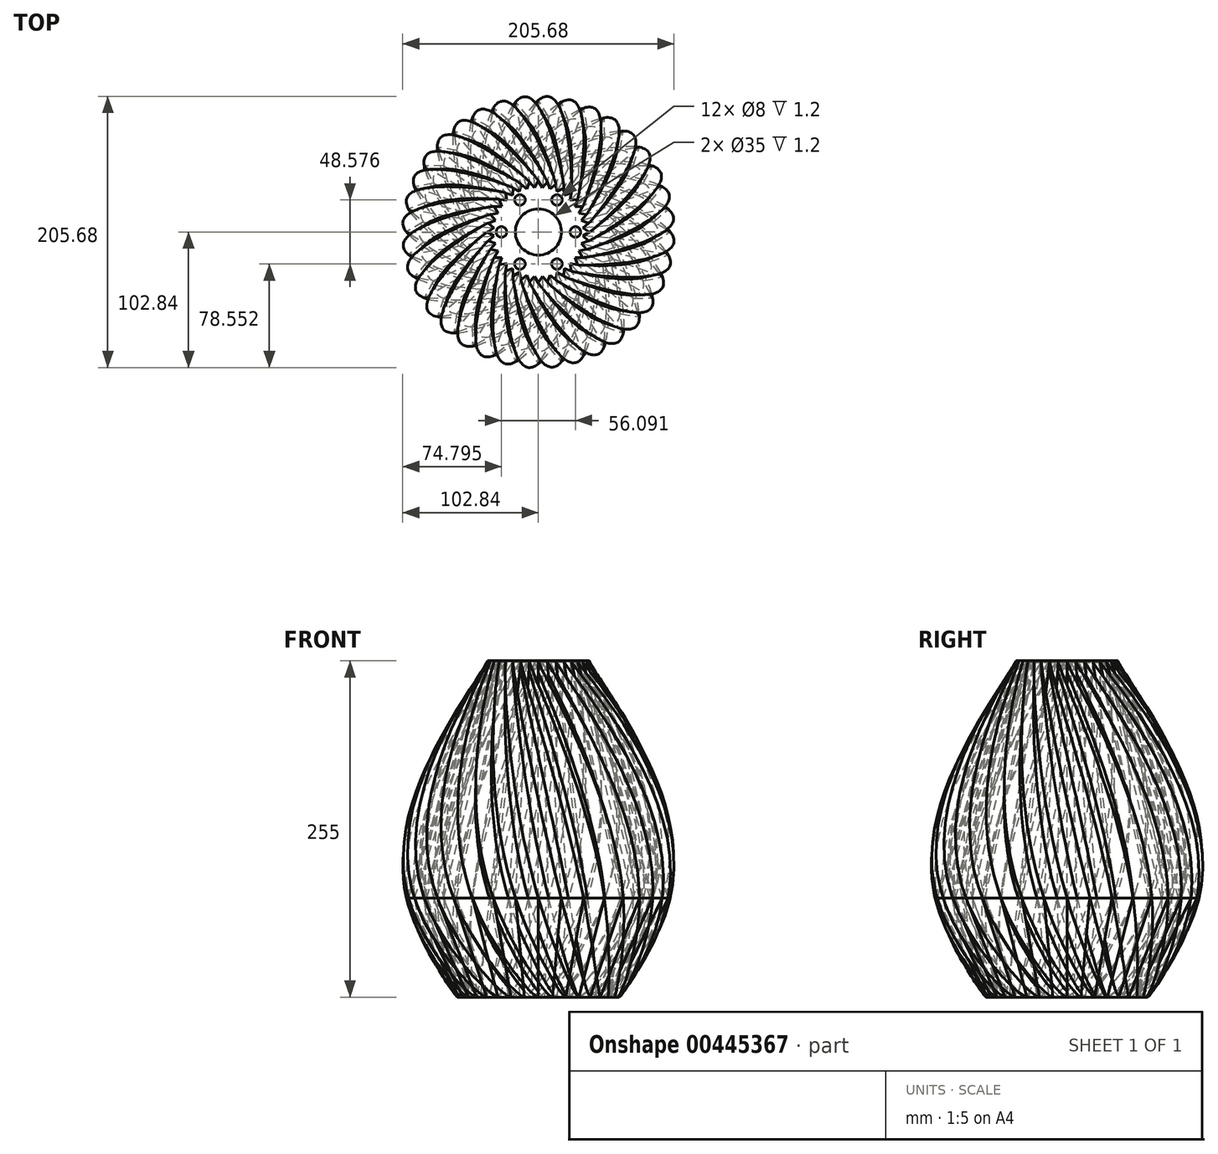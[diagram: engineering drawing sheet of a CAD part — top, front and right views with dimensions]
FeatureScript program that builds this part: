
annotation { "Feature Type Name" : "Feature", "Feature Type Description" : "" }
export const myFeature = defineFeature(function(context is Context, id is Id, definition is map)
    precondition{}
    {
        {
            var Q0;
            Q0=qCreatedBy(makeId("Top.planeOp"),FACE);
            var sketch = newSketch(context, id + "F0", { "sketchPlane" : qUnion([Q0])});
            skCircle(sketch, "E0", {"center": v(0, 0) * mm, "radius": 100 * mm, "construction": true});
            skLineSegment(sketch, "E1", {"start": v(-7.64, 87.34) * mm, "end": v(0, 100) * mm});
            skLineSegment(sketch, "E2.MirrorCS", {"start": v(7.64, 87.34) * mm, "end": v(0, 100) * mm});
            skLineSegment(sketch, "E3.1.0", {"start": v(-22.7, 84.69) * mm, "end": v(-17.36, 98.48) * mm});
            skLineSegment(sketch, "E3.1.1", {"start": v(-7.64, 87.34) * mm, "end": v(-17.36, 98.48) * mm});
            skLineSegment(sketch, "E3.2.0", {"start": v(-37.05, 79.46) * mm, "end": v(-34.2, 93.97) * mm});
            skLineSegment(sketch, "E3.2.1", {"start": v(-22.7, 84.69) * mm, "end": v(-34.2, 93.97) * mm});
            skLineSegment(sketch, "E3.3.0", {"start": v(-50.29, 71.82) * mm, "end": v(-50, 86.6) * mm});
            skLineSegment(sketch, "E3.3.1", {"start": v(-37.05, 79.46) * mm, "end": v(-50, 86.6) * mm});
            skLineSegment(sketch, "E3.4.0", {"start": v(-62, 62) * mm, "end": v(-64.28, 76.6) * mm});
            skLineSegment(sketch, "E3.4.1", {"start": v(-50.29, 71.82) * mm, "end": v(-64.28, 76.6) * mm});
            skLineSegment(sketch, "E3.5.0", {"start": v(-71.82, 50.29) * mm, "end": v(-76.6, 64.28) * mm});
            skLineSegment(sketch, "E3.5.1", {"start": v(-62, 62) * mm, "end": v(-76.6, 64.28) * mm});
            skLineSegment(sketch, "E3.6.0", {"start": v(-79.46, 37.05) * mm, "end": v(-86.6, 50) * mm});
            skLineSegment(sketch, "E3.6.1", {"start": v(-71.82, 50.29) * mm, "end": v(-86.6, 50) * mm});
            skLineSegment(sketch, "E3.7.0", {"start": v(-84.69, 22.7) * mm, "end": v(-93.97, 34.2) * mm});
            skLineSegment(sketch, "E3.7.1", {"start": v(-79.46, 37.05) * mm, "end": v(-93.97, 34.2) * mm});
            skLineSegment(sketch, "E3.8.0", {"start": v(-87.34, 7.64) * mm, "end": v(-98.48, 17.36) * mm});
            skLineSegment(sketch, "E3.8.1", {"start": v(-84.69, 22.7) * mm, "end": v(-98.48, 17.36) * mm});
            skLineSegment(sketch, "E3.9.0", {"start": v(-87.34, -7.64) * mm, "end": v(-100, 0) * mm});
            skLineSegment(sketch, "E3.9.1", {"start": v(-87.34, 7.64) * mm, "end": v(-100, 0) * mm});
            skLineSegment(sketch, "E3.10.0", {"start": v(-84.69, -22.7) * mm, "end": v(-98.48, -17.36) * mm});
            skLineSegment(sketch, "E3.10.1", {"start": v(-87.34, -7.64) * mm, "end": v(-98.48, -17.36) * mm});
            skLineSegment(sketch, "E3.11.0", {"start": v(-79.46, -37.05) * mm, "end": v(-93.97, -34.2) * mm});
            skLineSegment(sketch, "E3.11.1", {"start": v(-84.69, -22.7) * mm, "end": v(-93.97, -34.2) * mm});
            skLineSegment(sketch, "E3.12.0", {"start": v(-71.82, -50.29) * mm, "end": v(-86.6, -50) * mm});
            skLineSegment(sketch, "E3.12.1", {"start": v(-79.46, -37.05) * mm, "end": v(-86.6, -50) * mm});
            skLineSegment(sketch, "E3.13.0", {"start": v(-62, -62) * mm, "end": v(-76.6, -64.28) * mm});
            skLineSegment(sketch, "E3.13.1", {"start": v(-71.82, -50.29) * mm, "end": v(-76.6, -64.28) * mm});
            skLineSegment(sketch, "E3.14.0", {"start": v(-50.29, -71.82) * mm, "end": v(-64.28, -76.6) * mm});
            skLineSegment(sketch, "E3.14.1", {"start": v(-62, -62) * mm, "end": v(-64.28, -76.6) * mm});
            skLineSegment(sketch, "E3.15.0", {"start": v(-37.05, -79.46) * mm, "end": v(-50, -86.6) * mm});
            skLineSegment(sketch, "E3.15.1", {"start": v(-50.29, -71.82) * mm, "end": v(-50, -86.6) * mm});
            skLineSegment(sketch, "E3.16.0", {"start": v(-22.7, -84.69) * mm, "end": v(-34.2, -93.97) * mm});
            skLineSegment(sketch, "E3.16.1", {"start": v(-37.05, -79.46) * mm, "end": v(-34.2, -93.97) * mm});
            skLineSegment(sketch, "E3.17.0", {"start": v(-7.64, -87.34) * mm, "end": v(-17.36, -98.48) * mm});
            skLineSegment(sketch, "E3.17.1", {"start": v(-22.7, -84.69) * mm, "end": v(-17.36, -98.48) * mm});
            skLineSegment(sketch, "E3.18.0", {"start": v(7.64, -87.34) * mm, "end": v(0, -100) * mm});
            skLineSegment(sketch, "E3.18.1", {"start": v(-7.64, -87.34) * mm, "end": v(0, -100) * mm});
            skLineSegment(sketch, "E3.19.0", {"start": v(22.7, -84.69) * mm, "end": v(17.36, -98.48) * mm});
            skLineSegment(sketch, "E3.19.1", {"start": v(7.64, -87.34) * mm, "end": v(17.36, -98.48) * mm});
            skLineSegment(sketch, "E3.20.0", {"start": v(37.05, -79.46) * mm, "end": v(34.2, -93.97) * mm});
            skLineSegment(sketch, "E3.20.1", {"start": v(22.7, -84.69) * mm, "end": v(34.2, -93.97) * mm});
            skLineSegment(sketch, "E3.21.0", {"start": v(50.29, -71.82) * mm, "end": v(50, -86.6) * mm});
            skLineSegment(sketch, "E3.21.1", {"start": v(37.05, -79.46) * mm, "end": v(50, -86.6) * mm});
            skLineSegment(sketch, "E3.22.0", {"start": v(62, -62) * mm, "end": v(64.28, -76.6) * mm});
            skLineSegment(sketch, "E3.22.1", {"start": v(50.29, -71.82) * mm, "end": v(64.28, -76.6) * mm});
            skLineSegment(sketch, "E3.23.0", {"start": v(71.82, -50.29) * mm, "end": v(76.6, -64.28) * mm});
            skLineSegment(sketch, "E3.23.1", {"start": v(62, -62) * mm, "end": v(76.6, -64.28) * mm});
            skLineSegment(sketch, "E3.24.0", {"start": v(79.46, -37.05) * mm, "end": v(86.6, -50) * mm});
            skLineSegment(sketch, "E3.24.1", {"start": v(71.82, -50.29) * mm, "end": v(86.6, -50) * mm});
            skLineSegment(sketch, "E3.25.0", {"start": v(84.69, -22.7) * mm, "end": v(93.97, -34.2) * mm});
            skLineSegment(sketch, "E3.25.1", {"start": v(79.46, -37.05) * mm, "end": v(93.97, -34.2) * mm});
            skLineSegment(sketch, "E3.26.0", {"start": v(87.34, -7.64) * mm, "end": v(98.48, -17.36) * mm});
            skLineSegment(sketch, "E3.26.1", {"start": v(84.69, -22.7) * mm, "end": v(98.48, -17.36) * mm});
            skLineSegment(sketch, "E3.27.0", {"start": v(87.34, 7.64) * mm, "end": v(100, 0) * mm});
            skLineSegment(sketch, "E3.27.1", {"start": v(87.34, -7.64) * mm, "end": v(100, 0) * mm});
            skLineSegment(sketch, "E3.28.0", {"start": v(84.69, 22.7) * mm, "end": v(98.48, 17.36) * mm});
            skLineSegment(sketch, "E3.28.1", {"start": v(87.34, 7.64) * mm, "end": v(98.48, 17.36) * mm});
            skLineSegment(sketch, "E3.29.0", {"start": v(79.46, 37.05) * mm, "end": v(93.97, 34.2) * mm});
            skLineSegment(sketch, "E3.29.1", {"start": v(84.69, 22.7) * mm, "end": v(93.97, 34.2) * mm});
            skLineSegment(sketch, "E3.30.0", {"start": v(71.82, 50.29) * mm, "end": v(86.6, 50) * mm});
            skLineSegment(sketch, "E3.30.1", {"start": v(79.46, 37.05) * mm, "end": v(86.6, 50) * mm});
            skLineSegment(sketch, "E3.31.0", {"start": v(62, 62) * mm, "end": v(76.6, 64.28) * mm});
            skLineSegment(sketch, "E3.31.1", {"start": v(71.82, 50.29) * mm, "end": v(76.6, 64.28) * mm});
            skLineSegment(sketch, "E3.32.0", {"start": v(50.29, 71.82) * mm, "end": v(64.28, 76.6) * mm});
            skLineSegment(sketch, "E3.32.1", {"start": v(62, 62) * mm, "end": v(64.28, 76.6) * mm});
            skLineSegment(sketch, "E3.33.0", {"start": v(37.05, 79.46) * mm, "end": v(50, 86.6) * mm});
            skLineSegment(sketch, "E3.33.1", {"start": v(50.29, 71.82) * mm, "end": v(50, 86.6) * mm});
            skLineSegment(sketch, "E3.34.0", {"start": v(22.7, 84.69) * mm, "end": v(34.2, 93.97) * mm});
            skLineSegment(sketch, "E3.34.1", {"start": v(37.05, 79.46) * mm, "end": v(34.2, 93.97) * mm});
            skLineSegment(sketch, "E3.35.0", {"start": v(7.64, 87.34) * mm, "end": v(17.36, 98.48) * mm});
            skLineSegment(sketch, "E3.35.1", {"start": v(22.7, 84.69) * mm, "end": v(17.36, 98.48) * mm});
            skSolve(sketch);
        }
        {
            var Q0;
            Q0=makeQuery(id+"F0.imprint","IMPRINT",FACE,{"disambiguationData":[TD([[makeQuery(id+"F0.imprint","IMPRINT",EDGE,{"derivedFrom":sQuery(id+"F0.wireOp",EDGE,"E1")}),-1.0]])]});
            extrude(context, id + "F1", {"entities" : qUnion([Q0]), "depth" : 180 * mm, "hasDraft" : true, "draftAngle" : 10 * degree, "draftPullDirection" : true});
        }
        {
            var Q1;
            Q1=makeQuery(id+"F1.opExtrude","CAP_FACE",FACE,{"disambiguationData":[OSD([sQuery(id+"F0.wireOp",EDGE,"E1"),sQuery(id+"F0.wireOp",EDGE,"E2.MirrorCS"),sQuery(id+"F0.wireOp",EDGE,"E3.1.0"),sQuery(id+"F0.wireOp",EDGE,"E3.1.1"),sQuery(id+"F0.wireOp",EDGE,"E3.2.0"),sQuery(id+"F0.wireOp",EDGE,"E3.2.1"),sQuery(id+"F0.wireOp",EDGE,"E3.3.0"),sQuery(id+"F0.wireOp",EDGE,"E3.3.1"),sQuery(id+"F0.wireOp",EDGE,"E3.4.0"),sQuery(id+"F0.wireOp",EDGE,"E3.4.1"),sQuery(id+"F0.wireOp",EDGE,"E3.5.0"),sQuery(id+"F0.wireOp",EDGE,"E3.5.1"),sQuery(id+"F0.wireOp",EDGE,"E3.6.0"),sQuery(id+"F0.wireOp",EDGE,"E3.6.1"),sQuery(id+"F0.wireOp",EDGE,"E3.7.0"),sQuery(id+"F0.wireOp",EDGE,"E3.7.1"),sQuery(id+"F0.wireOp",EDGE,"E3.8.0"),sQuery(id+"F0.wireOp",EDGE,"E3.8.1"),sQuery(id+"F0.wireOp",EDGE,"E3.9.0"),sQuery(id+"F0.wireOp",EDGE,"E3.9.1"),sQuery(id+"F0.wireOp",EDGE,"E3.10.0"),sQuery(id+"F0.wireOp",EDGE,"E3.10.1"),sQuery(id+"F0.wireOp",EDGE,"E3.11.0"),sQuery(id+"F0.wireOp",EDGE,"E3.11.1"),sQuery(id+"F0.wireOp",EDGE,"E3.12.0"),sQuery(id+"F0.wireOp",EDGE,"E3.12.1"),sQuery(id+"F0.wireOp",EDGE,"E3.13.0"),sQuery(id+"F0.wireOp",EDGE,"E3.13.1"),sQuery(id+"F0.wireOp",EDGE,"E3.14.0"),sQuery(id+"F0.wireOp",EDGE,"E3.14.1"),sQuery(id+"F0.wireOp",EDGE,"E3.15.0"),sQuery(id+"F0.wireOp",EDGE,"E3.15.1"),sQuery(id+"F0.wireOp",EDGE,"E3.16.0"),sQuery(id+"F0.wireOp",EDGE,"E3.16.1"),sQuery(id+"F0.wireOp",EDGE,"E3.17.0"),sQuery(id+"F0.wireOp",EDGE,"E3.17.1"),sQuery(id+"F0.wireOp",EDGE,"E3.18.0"),sQuery(id+"F0.wireOp",EDGE,"E3.18.1"),sQuery(id+"F0.wireOp",EDGE,"E3.19.0"),sQuery(id+"F0.wireOp",EDGE,"E3.19.1"),sQuery(id+"F0.wireOp",EDGE,"E3.20.0"),sQuery(id+"F0.wireOp",EDGE,"E3.20.1"),sQuery(id+"F0.wireOp",EDGE,"E3.21.0"),sQuery(id+"F0.wireOp",EDGE,"E3.21.1"),sQuery(id+"F0.wireOp",EDGE,"E3.22.0"),sQuery(id+"F0.wireOp",EDGE,"E3.22.1"),sQuery(id+"F0.wireOp",EDGE,"E3.23.0"),sQuery(id+"F0.wireOp",EDGE,"E3.23.1"),sQuery(id+"F0.wireOp",EDGE,"E3.24.0"),sQuery(id+"F0.wireOp",EDGE,"E3.24.1"),sQuery(id+"F0.wireOp",EDGE,"E3.25.0"),sQuery(id+"F0.wireOp",EDGE,"E3.25.1"),sQuery(id+"F0.wireOp",EDGE,"E3.26.0"),sQuery(id+"F0.wireOp",EDGE,"E3.26.1"),sQuery(id+"F0.wireOp",EDGE,"E3.27.0"),sQuery(id+"F0.wireOp",EDGE,"E3.27.1"),sQuery(id+"F0.wireOp",EDGE,"E3.28.0"),sQuery(id+"F0.wireOp",EDGE,"E3.28.1"),sQuery(id+"F0.wireOp",EDGE,"E3.29.0"),sQuery(id+"F0.wireOp",EDGE,"E3.29.1"),sQuery(id+"F0.wireOp",EDGE,"E3.30.0"),sQuery(id+"F0.wireOp",EDGE,"E3.30.1"),sQuery(id+"F0.wireOp",EDGE,"E3.31.0"),sQuery(id+"F0.wireOp",EDGE,"E3.31.1"),sQuery(id+"F0.wireOp",EDGE,"E3.32.0"),sQuery(id+"F0.wireOp",EDGE,"E3.32.1"),sQuery(id+"F0.wireOp",EDGE,"E3.33.0"),sQuery(id+"F0.wireOp",EDGE,"E3.33.1"),sQuery(id+"F0.wireOp",EDGE,"E3.34.0"),sQuery(id+"F0.wireOp",EDGE,"E3.34.1"),sQuery(id+"F0.wireOp",EDGE,"E3.35.0"),sQuery(id+"F0.wireOp",EDGE,"E3.35.1")])],"isStart":false});
            var Q2;
            Q2=makeQuery(id+"F1.opExtrude","CAP_FACE",FACE,{"disambiguationData":[OSD([sQuery(id+"F0.wireOp",EDGE,"E1"),sQuery(id+"F0.wireOp",EDGE,"E2.MirrorCS"),sQuery(id+"F0.wireOp",EDGE,"E3.1.0"),sQuery(id+"F0.wireOp",EDGE,"E3.1.1"),sQuery(id+"F0.wireOp",EDGE,"E3.2.0"),sQuery(id+"F0.wireOp",EDGE,"E3.2.1"),sQuery(id+"F0.wireOp",EDGE,"E3.3.0"),sQuery(id+"F0.wireOp",EDGE,"E3.3.1"),sQuery(id+"F0.wireOp",EDGE,"E3.4.0"),sQuery(id+"F0.wireOp",EDGE,"E3.4.1"),sQuery(id+"F0.wireOp",EDGE,"E3.5.0"),sQuery(id+"F0.wireOp",EDGE,"E3.5.1"),sQuery(id+"F0.wireOp",EDGE,"E3.6.0"),sQuery(id+"F0.wireOp",EDGE,"E3.6.1"),sQuery(id+"F0.wireOp",EDGE,"E3.7.0"),sQuery(id+"F0.wireOp",EDGE,"E3.7.1"),sQuery(id+"F0.wireOp",EDGE,"E3.8.0"),sQuery(id+"F0.wireOp",EDGE,"E3.8.1"),sQuery(id+"F0.wireOp",EDGE,"E3.9.0"),sQuery(id+"F0.wireOp",EDGE,"E3.9.1"),sQuery(id+"F0.wireOp",EDGE,"E3.10.0"),sQuery(id+"F0.wireOp",EDGE,"E3.10.1"),sQuery(id+"F0.wireOp",EDGE,"E3.11.0"),sQuery(id+"F0.wireOp",EDGE,"E3.11.1"),sQuery(id+"F0.wireOp",EDGE,"E3.12.0"),sQuery(id+"F0.wireOp",EDGE,"E3.12.1"),sQuery(id+"F0.wireOp",EDGE,"E3.13.0"),sQuery(id+"F0.wireOp",EDGE,"E3.13.1"),sQuery(id+"F0.wireOp",EDGE,"E3.14.0"),sQuery(id+"F0.wireOp",EDGE,"E3.14.1"),sQuery(id+"F0.wireOp",EDGE,"E3.15.0"),sQuery(id+"F0.wireOp",EDGE,"E3.15.1"),sQuery(id+"F0.wireOp",EDGE,"E3.16.0"),sQuery(id+"F0.wireOp",EDGE,"E3.16.1"),sQuery(id+"F0.wireOp",EDGE,"E3.17.0"),sQuery(id+"F0.wireOp",EDGE,"E3.17.1"),sQuery(id+"F0.wireOp",EDGE,"E3.18.0"),sQuery(id+"F0.wireOp",EDGE,"E3.18.1"),sQuery(id+"F0.wireOp",EDGE,"E3.19.0"),sQuery(id+"F0.wireOp",EDGE,"E3.19.1"),sQuery(id+"F0.wireOp",EDGE,"E3.20.0"),sQuery(id+"F0.wireOp",EDGE,"E3.20.1"),sQuery(id+"F0.wireOp",EDGE,"E3.21.0"),sQuery(id+"F0.wireOp",EDGE,"E3.21.1"),sQuery(id+"F0.wireOp",EDGE,"E3.22.0"),sQuery(id+"F0.wireOp",EDGE,"E3.22.1"),sQuery(id+"F0.wireOp",EDGE,"E3.23.0"),sQuery(id+"F0.wireOp",EDGE,"E3.23.1"),sQuery(id+"F0.wireOp",EDGE,"E3.24.0"),sQuery(id+"F0.wireOp",EDGE,"E3.24.1"),sQuery(id+"F0.wireOp",EDGE,"E3.25.0"),sQuery(id+"F0.wireOp",EDGE,"E3.25.1"),sQuery(id+"F0.wireOp",EDGE,"E3.26.0"),sQuery(id+"F0.wireOp",EDGE,"E3.26.1"),sQuery(id+"F0.wireOp",EDGE,"E3.27.0"),sQuery(id+"F0.wireOp",EDGE,"E3.27.1"),sQuery(id+"F0.wireOp",EDGE,"E3.28.0"),sQuery(id+"F0.wireOp",EDGE,"E3.28.1"),sQuery(id+"F0.wireOp",EDGE,"E3.29.0"),sQuery(id+"F0.wireOp",EDGE,"E3.29.1"),sQuery(id+"F0.wireOp",EDGE,"E3.30.0"),sQuery(id+"F0.wireOp",EDGE,"E3.30.1"),sQuery(id+"F0.wireOp",EDGE,"E3.31.0"),sQuery(id+"F0.wireOp",EDGE,"E3.31.1"),sQuery(id+"F0.wireOp",EDGE,"E3.32.0"),sQuery(id+"F0.wireOp",EDGE,"E3.32.1"),sQuery(id+"F0.wireOp",EDGE,"E3.33.0"),sQuery(id+"F0.wireOp",EDGE,"E3.33.1"),sQuery(id+"F0.wireOp",EDGE,"E3.34.0"),sQuery(id+"F0.wireOp",EDGE,"E3.34.1"),sQuery(id+"F0.wireOp",EDGE,"E3.35.0"),sQuery(id+"F0.wireOp",EDGE,"E3.35.1")])],"isStart":true});
            var Q3;
            Q3=makeQuery(id+"F1.opExtrude","CAP_VERTEX",VERTEX,{"disambiguationData":[OSD([sQuery(id+"F0.wireOp",EDGE,"E3.18.0"),sQuery(id+"F0.wireOp",EDGE,"E3.18.1")])],"isStart":true});
            var Q4;
            Q4=makeQuery(id+"F1.opExtrude","CAP_VERTEX",VERTEX,{"disambiguationData":[OSD([sQuery(id+"F0.wireOp",EDGE,"E3.22.0"),sQuery(id+"F0.wireOp",EDGE,"E3.22.1")])],"isStart":false});
            loft(context, id + "F2", {"endCondition" : LoftEndDerivativeType.NORMAL_TO_PROFILE, "endMagnitude" : 2, "sheetProfilesArray" : [{ "sheetProfileEntities" : qUnion([Q1]) }, { "sheetProfileEntities" : qUnion([Q2]) }], "matchConnections" : true, "connections" : [{ "connectionEntities" : qUnion([Q3, Q4]), "connectionEdgeQueries" : qUnion([]), "connectionEdgeParameters" : [] }]});
        }
        {
            var Q0;
            Q0=makeQuery(id+"F2.opLoft","SWEPT_BODY",BODY,{"disambiguationData":[OSD([sQuery(id+"F0.wireOp",EDGE,"E1"),sQuery(id+"F0.wireOp",EDGE,"E2.MirrorCS"),sQuery(id+"F0.wireOp",EDGE,"E3.1.0"),sQuery(id+"F0.wireOp",EDGE,"E3.1.1"),sQuery(id+"F0.wireOp",EDGE,"E3.2.0"),sQuery(id+"F0.wireOp",EDGE,"E3.2.1"),sQuery(id+"F0.wireOp",EDGE,"E3.3.0"),sQuery(id+"F0.wireOp",EDGE,"E3.3.1"),sQuery(id+"F0.wireOp",EDGE,"E3.4.0"),sQuery(id+"F0.wireOp",EDGE,"E3.4.1"),sQuery(id+"F0.wireOp",EDGE,"E3.5.0"),sQuery(id+"F0.wireOp",EDGE,"E3.5.1"),sQuery(id+"F0.wireOp",EDGE,"E3.6.0"),sQuery(id+"F0.wireOp",EDGE,"E3.6.1"),sQuery(id+"F0.wireOp",EDGE,"E3.7.0"),sQuery(id+"F0.wireOp",EDGE,"E3.7.1"),sQuery(id+"F0.wireOp",EDGE,"E3.8.0"),sQuery(id+"F0.wireOp",EDGE,"E3.8.1"),sQuery(id+"F0.wireOp",EDGE,"E3.9.0"),sQuery(id+"F0.wireOp",EDGE,"E3.9.1"),sQuery(id+"F0.wireOp",EDGE,"E3.10.0"),sQuery(id+"F0.wireOp",EDGE,"E3.10.1"),sQuery(id+"F0.wireOp",EDGE,"E3.11.0"),sQuery(id+"F0.wireOp",EDGE,"E3.11.1"),sQuery(id+"F0.wireOp",EDGE,"E3.12.0"),sQuery(id+"F0.wireOp",EDGE,"E3.12.1"),sQuery(id+"F0.wireOp",EDGE,"E3.13.0"),sQuery(id+"F0.wireOp",EDGE,"E3.13.1"),sQuery(id+"F0.wireOp",EDGE,"E3.14.0"),sQuery(id+"F0.wireOp",EDGE,"E3.14.1"),sQuery(id+"F0.wireOp",EDGE,"E3.15.0"),sQuery(id+"F0.wireOp",EDGE,"E3.15.1"),sQuery(id+"F0.wireOp",EDGE,"E3.16.0"),sQuery(id+"F0.wireOp",EDGE,"E3.16.1"),sQuery(id+"F0.wireOp",EDGE,"E3.17.0"),sQuery(id+"F0.wireOp",EDGE,"E3.17.1"),sQuery(id+"F0.wireOp",EDGE,"E3.18.0"),sQuery(id+"F0.wireOp",EDGE,"E3.18.1"),sQuery(id+"F0.wireOp",EDGE,"E3.19.0"),sQuery(id+"F0.wireOp",EDGE,"E3.19.1"),sQuery(id+"F0.wireOp",EDGE,"E3.20.0"),sQuery(id+"F0.wireOp",EDGE,"E3.20.1"),sQuery(id+"F0.wireOp",EDGE,"E3.21.0"),sQuery(id+"F0.wireOp",EDGE,"E3.21.1"),sQuery(id+"F0.wireOp",EDGE,"E3.22.0"),sQuery(id+"F0.wireOp",EDGE,"E3.22.1"),sQuery(id+"F0.wireOp",EDGE,"E3.23.0"),sQuery(id+"F0.wireOp",EDGE,"E3.23.1"),sQuery(id+"F0.wireOp",EDGE,"E3.24.0"),sQuery(id+"F0.wireOp",EDGE,"E3.24.1"),sQuery(id+"F0.wireOp",EDGE,"E3.25.0"),sQuery(id+"F0.wireOp",EDGE,"E3.25.1"),sQuery(id+"F0.wireOp",EDGE,"E3.26.0"),sQuery(id+"F0.wireOp",EDGE,"E3.26.1"),sQuery(id+"F0.wireOp",EDGE,"E3.27.0"),sQuery(id+"F0.wireOp",EDGE,"E3.27.1"),sQuery(id+"F0.wireOp",EDGE,"E3.28.0"),sQuery(id+"F0.wireOp",EDGE,"E3.28.1"),sQuery(id+"F0.wireOp",EDGE,"E3.29.0"),sQuery(id+"F0.wireOp",EDGE,"E3.29.1"),sQuery(id+"F0.wireOp",EDGE,"E3.30.0"),sQuery(id+"F0.wireOp",EDGE,"E3.30.1"),sQuery(id+"F0.wireOp",EDGE,"E3.31.0"),sQuery(id+"F0.wireOp",EDGE,"E3.31.1"),sQuery(id+"F0.wireOp",EDGE,"E3.32.0"),sQuery(id+"F0.wireOp",EDGE,"E3.32.1"),sQuery(id+"F0.wireOp",EDGE,"E3.33.0"),sQuery(id+"F0.wireOp",EDGE,"E3.33.1"),sQuery(id+"F0.wireOp",EDGE,"E3.34.0"),sQuery(id+"F0.wireOp",EDGE,"E3.34.1"),sQuery(id+"F0.wireOp",EDGE,"E3.35.0"),sQuery(id+"F0.wireOp",EDGE,"E3.35.1")])]});
            deleteBodies(context, id + "F3", {"entities" : qUnion([Q0])});
        }
        {
            var Q0;
            Q0=makeQuery(id+"F1.opExtrude","CAP_FACE",FACE,{"disambiguationData":[OSD([sQuery(id+"F0.wireOp",EDGE,"E1"),sQuery(id+"F0.wireOp",EDGE,"E2.MirrorCS"),sQuery(id+"F0.wireOp",EDGE,"E3.1.0"),sQuery(id+"F0.wireOp",EDGE,"E3.1.1"),sQuery(id+"F0.wireOp",EDGE,"E3.2.0"),sQuery(id+"F0.wireOp",EDGE,"E3.2.1"),sQuery(id+"F0.wireOp",EDGE,"E3.3.0"),sQuery(id+"F0.wireOp",EDGE,"E3.3.1"),sQuery(id+"F0.wireOp",EDGE,"E3.4.0"),sQuery(id+"F0.wireOp",EDGE,"E3.4.1"),sQuery(id+"F0.wireOp",EDGE,"E3.5.0"),sQuery(id+"F0.wireOp",EDGE,"E3.5.1"),sQuery(id+"F0.wireOp",EDGE,"E3.6.0"),sQuery(id+"F0.wireOp",EDGE,"E3.6.1"),sQuery(id+"F0.wireOp",EDGE,"E3.7.0"),sQuery(id+"F0.wireOp",EDGE,"E3.7.1"),sQuery(id+"F0.wireOp",EDGE,"E3.8.0"),sQuery(id+"F0.wireOp",EDGE,"E3.8.1"),sQuery(id+"F0.wireOp",EDGE,"E3.9.0"),sQuery(id+"F0.wireOp",EDGE,"E3.9.1"),sQuery(id+"F0.wireOp",EDGE,"E3.10.0"),sQuery(id+"F0.wireOp",EDGE,"E3.10.1"),sQuery(id+"F0.wireOp",EDGE,"E3.11.0"),sQuery(id+"F0.wireOp",EDGE,"E3.11.1"),sQuery(id+"F0.wireOp",EDGE,"E3.12.0"),sQuery(id+"F0.wireOp",EDGE,"E3.12.1"),sQuery(id+"F0.wireOp",EDGE,"E3.13.0"),sQuery(id+"F0.wireOp",EDGE,"E3.13.1"),sQuery(id+"F0.wireOp",EDGE,"E3.14.0"),sQuery(id+"F0.wireOp",EDGE,"E3.14.1"),sQuery(id+"F0.wireOp",EDGE,"E3.15.0"),sQuery(id+"F0.wireOp",EDGE,"E3.15.1"),sQuery(id+"F0.wireOp",EDGE,"E3.16.0"),sQuery(id+"F0.wireOp",EDGE,"E3.16.1"),sQuery(id+"F0.wireOp",EDGE,"E3.17.0"),sQuery(id+"F0.wireOp",EDGE,"E3.17.1"),sQuery(id+"F0.wireOp",EDGE,"E3.18.0"),sQuery(id+"F0.wireOp",EDGE,"E3.18.1"),sQuery(id+"F0.wireOp",EDGE,"E3.19.0"),sQuery(id+"F0.wireOp",EDGE,"E3.19.1"),sQuery(id+"F0.wireOp",EDGE,"E3.20.0"),sQuery(id+"F0.wireOp",EDGE,"E3.20.1"),sQuery(id+"F0.wireOp",EDGE,"E3.21.0"),sQuery(id+"F0.wireOp",EDGE,"E3.21.1"),sQuery(id+"F0.wireOp",EDGE,"E3.22.0"),sQuery(id+"F0.wireOp",EDGE,"E3.22.1"),sQuery(id+"F0.wireOp",EDGE,"E3.23.0"),sQuery(id+"F0.wireOp",EDGE,"E3.23.1"),sQuery(id+"F0.wireOp",EDGE,"E3.24.0"),sQuery(id+"F0.wireOp",EDGE,"E3.24.1"),sQuery(id+"F0.wireOp",EDGE,"E3.25.0"),sQuery(id+"F0.wireOp",EDGE,"E3.25.1"),sQuery(id+"F0.wireOp",EDGE,"E3.26.0"),sQuery(id+"F0.wireOp",EDGE,"E3.26.1"),sQuery(id+"F0.wireOp",EDGE,"E3.27.0"),sQuery(id+"F0.wireOp",EDGE,"E3.27.1"),sQuery(id+"F0.wireOp",EDGE,"E3.28.0"),sQuery(id+"F0.wireOp",EDGE,"E3.28.1"),sQuery(id+"F0.wireOp",EDGE,"E3.29.0"),sQuery(id+"F0.wireOp",EDGE,"E3.29.1"),sQuery(id+"F0.wireOp",EDGE,"E3.30.0"),sQuery(id+"F0.wireOp",EDGE,"E3.30.1"),sQuery(id+"F0.wireOp",EDGE,"E3.31.0"),sQuery(id+"F0.wireOp",EDGE,"E3.31.1"),sQuery(id+"F0.wireOp",EDGE,"E3.32.0"),sQuery(id+"F0.wireOp",EDGE,"E3.32.1"),sQuery(id+"F0.wireOp",EDGE,"E3.33.0"),sQuery(id+"F0.wireOp",EDGE,"E3.33.1"),sQuery(id+"F0.wireOp",EDGE,"E3.34.0"),sQuery(id+"F0.wireOp",EDGE,"E3.34.1"),sQuery(id+"F0.wireOp",EDGE,"E3.35.0"),sQuery(id+"F0.wireOp",EDGE,"E3.35.1")])],"isStart":true});
            extrude(context, id + "F4", {"entities" : qUnion([Q0]), "depth" : 75 * mm, "hasDraft" : true, "draftAngle" : 15 * degree, "draftPullDirection" : true});
        }
        {
            var Q1;
            Q1=makeQuery(id+"F1.opExtrude","CAP_FACE",FACE,{"disambiguationData":[OSD([sQuery(id+"F0.wireOp",EDGE,"E1"),sQuery(id+"F0.wireOp",EDGE,"E2.MirrorCS"),sQuery(id+"F0.wireOp",EDGE,"E3.1.0"),sQuery(id+"F0.wireOp",EDGE,"E3.1.1"),sQuery(id+"F0.wireOp",EDGE,"E3.2.0"),sQuery(id+"F0.wireOp",EDGE,"E3.2.1"),sQuery(id+"F0.wireOp",EDGE,"E3.3.0"),sQuery(id+"F0.wireOp",EDGE,"E3.3.1"),sQuery(id+"F0.wireOp",EDGE,"E3.4.0"),sQuery(id+"F0.wireOp",EDGE,"E3.4.1"),sQuery(id+"F0.wireOp",EDGE,"E3.5.0"),sQuery(id+"F0.wireOp",EDGE,"E3.5.1"),sQuery(id+"F0.wireOp",EDGE,"E3.6.0"),sQuery(id+"F0.wireOp",EDGE,"E3.6.1"),sQuery(id+"F0.wireOp",EDGE,"E3.7.0"),sQuery(id+"F0.wireOp",EDGE,"E3.7.1"),sQuery(id+"F0.wireOp",EDGE,"E3.8.0"),sQuery(id+"F0.wireOp",EDGE,"E3.8.1"),sQuery(id+"F0.wireOp",EDGE,"E3.9.0"),sQuery(id+"F0.wireOp",EDGE,"E3.9.1"),sQuery(id+"F0.wireOp",EDGE,"E3.10.0"),sQuery(id+"F0.wireOp",EDGE,"E3.10.1"),sQuery(id+"F0.wireOp",EDGE,"E3.11.0"),sQuery(id+"F0.wireOp",EDGE,"E3.11.1"),sQuery(id+"F0.wireOp",EDGE,"E3.12.0"),sQuery(id+"F0.wireOp",EDGE,"E3.12.1"),sQuery(id+"F0.wireOp",EDGE,"E3.13.0"),sQuery(id+"F0.wireOp",EDGE,"E3.13.1"),sQuery(id+"F0.wireOp",EDGE,"E3.14.0"),sQuery(id+"F0.wireOp",EDGE,"E3.14.1"),sQuery(id+"F0.wireOp",EDGE,"E3.15.0"),sQuery(id+"F0.wireOp",EDGE,"E3.15.1"),sQuery(id+"F0.wireOp",EDGE,"E3.16.0"),sQuery(id+"F0.wireOp",EDGE,"E3.16.1"),sQuery(id+"F0.wireOp",EDGE,"E3.17.0"),sQuery(id+"F0.wireOp",EDGE,"E3.17.1"),sQuery(id+"F0.wireOp",EDGE,"E3.18.0"),sQuery(id+"F0.wireOp",EDGE,"E3.18.1"),sQuery(id+"F0.wireOp",EDGE,"E3.19.0"),sQuery(id+"F0.wireOp",EDGE,"E3.19.1"),sQuery(id+"F0.wireOp",EDGE,"E3.20.0"),sQuery(id+"F0.wireOp",EDGE,"E3.20.1"),sQuery(id+"F0.wireOp",EDGE,"E3.21.0"),sQuery(id+"F0.wireOp",EDGE,"E3.21.1"),sQuery(id+"F0.wireOp",EDGE,"E3.22.0"),sQuery(id+"F0.wireOp",EDGE,"E3.22.1"),sQuery(id+"F0.wireOp",EDGE,"E3.23.0"),sQuery(id+"F0.wireOp",EDGE,"E3.23.1"),sQuery(id+"F0.wireOp",EDGE,"E3.24.0"),sQuery(id+"F0.wireOp",EDGE,"E3.24.1"),sQuery(id+"F0.wireOp",EDGE,"E3.25.0"),sQuery(id+"F0.wireOp",EDGE,"E3.25.1"),sQuery(id+"F0.wireOp",EDGE,"E3.26.0"),sQuery(id+"F0.wireOp",EDGE,"E3.26.1"),sQuery(id+"F0.wireOp",EDGE,"E3.27.0"),sQuery(id+"F0.wireOp",EDGE,"E3.27.1"),sQuery(id+"F0.wireOp",EDGE,"E3.28.0"),sQuery(id+"F0.wireOp",EDGE,"E3.28.1"),sQuery(id+"F0.wireOp",EDGE,"E3.29.0"),sQuery(id+"F0.wireOp",EDGE,"E3.29.1"),sQuery(id+"F0.wireOp",EDGE,"E3.30.0"),sQuery(id+"F0.wireOp",EDGE,"E3.30.1"),sQuery(id+"F0.wireOp",EDGE,"E3.31.0"),sQuery(id+"F0.wireOp",EDGE,"E3.31.1"),sQuery(id+"F0.wireOp",EDGE,"E3.32.0"),sQuery(id+"F0.wireOp",EDGE,"E3.32.1"),sQuery(id+"F0.wireOp",EDGE,"E3.33.0"),sQuery(id+"F0.wireOp",EDGE,"E3.33.1"),sQuery(id+"F0.wireOp",EDGE,"E3.34.0"),sQuery(id+"F0.wireOp",EDGE,"E3.34.1"),sQuery(id+"F0.wireOp",EDGE,"E3.35.0"),sQuery(id+"F0.wireOp",EDGE,"E3.35.1")])],"isStart":false});
            var Q2;
            Q2=makeQuery(id+"F1.opExtrude","CAP_FACE",FACE,{"disambiguationData":[OSD([sQuery(id+"F0.wireOp",EDGE,"E1"),sQuery(id+"F0.wireOp",EDGE,"E2.MirrorCS"),sQuery(id+"F0.wireOp",EDGE,"E3.1.0"),sQuery(id+"F0.wireOp",EDGE,"E3.1.1"),sQuery(id+"F0.wireOp",EDGE,"E3.2.0"),sQuery(id+"F0.wireOp",EDGE,"E3.2.1"),sQuery(id+"F0.wireOp",EDGE,"E3.3.0"),sQuery(id+"F0.wireOp",EDGE,"E3.3.1"),sQuery(id+"F0.wireOp",EDGE,"E3.4.0"),sQuery(id+"F0.wireOp",EDGE,"E3.4.1"),sQuery(id+"F0.wireOp",EDGE,"E3.5.0"),sQuery(id+"F0.wireOp",EDGE,"E3.5.1"),sQuery(id+"F0.wireOp",EDGE,"E3.6.0"),sQuery(id+"F0.wireOp",EDGE,"E3.6.1"),sQuery(id+"F0.wireOp",EDGE,"E3.7.0"),sQuery(id+"F0.wireOp",EDGE,"E3.7.1"),sQuery(id+"F0.wireOp",EDGE,"E3.8.0"),sQuery(id+"F0.wireOp",EDGE,"E3.8.1"),sQuery(id+"F0.wireOp",EDGE,"E3.9.0"),sQuery(id+"F0.wireOp",EDGE,"E3.9.1"),sQuery(id+"F0.wireOp",EDGE,"E3.10.0"),sQuery(id+"F0.wireOp",EDGE,"E3.10.1"),sQuery(id+"F0.wireOp",EDGE,"E3.11.0"),sQuery(id+"F0.wireOp",EDGE,"E3.11.1"),sQuery(id+"F0.wireOp",EDGE,"E3.12.0"),sQuery(id+"F0.wireOp",EDGE,"E3.12.1"),sQuery(id+"F0.wireOp",EDGE,"E3.13.0"),sQuery(id+"F0.wireOp",EDGE,"E3.13.1"),sQuery(id+"F0.wireOp",EDGE,"E3.14.0"),sQuery(id+"F0.wireOp",EDGE,"E3.14.1"),sQuery(id+"F0.wireOp",EDGE,"E3.15.0"),sQuery(id+"F0.wireOp",EDGE,"E3.15.1"),sQuery(id+"F0.wireOp",EDGE,"E3.16.0"),sQuery(id+"F0.wireOp",EDGE,"E3.16.1"),sQuery(id+"F0.wireOp",EDGE,"E3.17.0"),sQuery(id+"F0.wireOp",EDGE,"E3.17.1"),sQuery(id+"F0.wireOp",EDGE,"E3.18.0"),sQuery(id+"F0.wireOp",EDGE,"E3.18.1"),sQuery(id+"F0.wireOp",EDGE,"E3.19.0"),sQuery(id+"F0.wireOp",EDGE,"E3.19.1"),sQuery(id+"F0.wireOp",EDGE,"E3.20.0"),sQuery(id+"F0.wireOp",EDGE,"E3.20.1"),sQuery(id+"F0.wireOp",EDGE,"E3.21.0"),sQuery(id+"F0.wireOp",EDGE,"E3.21.1"),sQuery(id+"F0.wireOp",EDGE,"E3.22.0"),sQuery(id+"F0.wireOp",EDGE,"E3.22.1"),sQuery(id+"F0.wireOp",EDGE,"E3.23.0"),sQuery(id+"F0.wireOp",EDGE,"E3.23.1"),sQuery(id+"F0.wireOp",EDGE,"E3.24.0"),sQuery(id+"F0.wireOp",EDGE,"E3.24.1"),sQuery(id+"F0.wireOp",EDGE,"E3.25.0"),sQuery(id+"F0.wireOp",EDGE,"E3.25.1"),sQuery(id+"F0.wireOp",EDGE,"E3.26.0"),sQuery(id+"F0.wireOp",EDGE,"E3.26.1"),sQuery(id+"F0.wireOp",EDGE,"E3.27.0"),sQuery(id+"F0.wireOp",EDGE,"E3.27.1"),sQuery(id+"F0.wireOp",EDGE,"E3.28.0"),sQuery(id+"F0.wireOp",EDGE,"E3.28.1"),sQuery(id+"F0.wireOp",EDGE,"E3.29.0"),sQuery(id+"F0.wireOp",EDGE,"E3.29.1"),sQuery(id+"F0.wireOp",EDGE,"E3.30.0"),sQuery(id+"F0.wireOp",EDGE,"E3.30.1"),sQuery(id+"F0.wireOp",EDGE,"E3.31.0"),sQuery(id+"F0.wireOp",EDGE,"E3.31.1"),sQuery(id+"F0.wireOp",EDGE,"E3.32.0"),sQuery(id+"F0.wireOp",EDGE,"E3.32.1"),sQuery(id+"F0.wireOp",EDGE,"E3.33.0"),sQuery(id+"F0.wireOp",EDGE,"E3.33.1"),sQuery(id+"F0.wireOp",EDGE,"E3.34.0"),sQuery(id+"F0.wireOp",EDGE,"E3.34.1"),sQuery(id+"F0.wireOp",EDGE,"E3.35.0"),sQuery(id+"F0.wireOp",EDGE,"E3.35.1")])],"isStart":true});
            var Q3;
            Q3=makeQuery(id+"F4.opExtrude","CAP_FACE",FACE,{"disambiguationData":[OSD([sQuery(id+"F0.wireOp",EDGE,"E1"),sQuery(id+"F0.wireOp",EDGE,"E2.MirrorCS"),sQuery(id+"F0.wireOp",EDGE,"E3.1.0"),sQuery(id+"F0.wireOp",EDGE,"E3.1.1"),sQuery(id+"F0.wireOp",EDGE,"E3.2.0"),sQuery(id+"F0.wireOp",EDGE,"E3.2.1"),sQuery(id+"F0.wireOp",EDGE,"E3.3.0"),sQuery(id+"F0.wireOp",EDGE,"E3.3.1"),sQuery(id+"F0.wireOp",EDGE,"E3.4.0"),sQuery(id+"F0.wireOp",EDGE,"E3.4.1"),sQuery(id+"F0.wireOp",EDGE,"E3.5.0"),sQuery(id+"F0.wireOp",EDGE,"E3.5.1"),sQuery(id+"F0.wireOp",EDGE,"E3.6.0"),sQuery(id+"F0.wireOp",EDGE,"E3.6.1"),sQuery(id+"F0.wireOp",EDGE,"E3.7.0"),sQuery(id+"F0.wireOp",EDGE,"E3.7.1"),sQuery(id+"F0.wireOp",EDGE,"E3.8.0"),sQuery(id+"F0.wireOp",EDGE,"E3.8.1"),sQuery(id+"F0.wireOp",EDGE,"E3.9.0"),sQuery(id+"F0.wireOp",EDGE,"E3.9.1"),sQuery(id+"F0.wireOp",EDGE,"E3.10.0"),sQuery(id+"F0.wireOp",EDGE,"E3.10.1"),sQuery(id+"F0.wireOp",EDGE,"E3.11.0"),sQuery(id+"F0.wireOp",EDGE,"E3.11.1"),sQuery(id+"F0.wireOp",EDGE,"E3.12.0"),sQuery(id+"F0.wireOp",EDGE,"E3.12.1"),sQuery(id+"F0.wireOp",EDGE,"E3.13.0"),sQuery(id+"F0.wireOp",EDGE,"E3.13.1"),sQuery(id+"F0.wireOp",EDGE,"E3.14.0"),sQuery(id+"F0.wireOp",EDGE,"E3.14.1"),sQuery(id+"F0.wireOp",EDGE,"E3.15.0"),sQuery(id+"F0.wireOp",EDGE,"E3.15.1"),sQuery(id+"F0.wireOp",EDGE,"E3.16.0"),sQuery(id+"F0.wireOp",EDGE,"E3.16.1"),sQuery(id+"F0.wireOp",EDGE,"E3.17.0"),sQuery(id+"F0.wireOp",EDGE,"E3.17.1"),sQuery(id+"F0.wireOp",EDGE,"E3.18.0"),sQuery(id+"F0.wireOp",EDGE,"E3.18.1"),sQuery(id+"F0.wireOp",EDGE,"E3.19.0"),sQuery(id+"F0.wireOp",EDGE,"E3.19.1"),sQuery(id+"F0.wireOp",EDGE,"E3.20.0"),sQuery(id+"F0.wireOp",EDGE,"E3.20.1"),sQuery(id+"F0.wireOp",EDGE,"E3.21.0"),sQuery(id+"F0.wireOp",EDGE,"E3.21.1"),sQuery(id+"F0.wireOp",EDGE,"E3.22.0"),sQuery(id+"F0.wireOp",EDGE,"E3.22.1"),sQuery(id+"F0.wireOp",EDGE,"E3.23.0"),sQuery(id+"F0.wireOp",EDGE,"E3.23.1"),sQuery(id+"F0.wireOp",EDGE,"E3.24.0"),sQuery(id+"F0.wireOp",EDGE,"E3.24.1"),sQuery(id+"F0.wireOp",EDGE,"E3.25.0"),sQuery(id+"F0.wireOp",EDGE,"E3.25.1"),sQuery(id+"F0.wireOp",EDGE,"E3.26.0"),sQuery(id+"F0.wireOp",EDGE,"E3.26.1"),sQuery(id+"F0.wireOp",EDGE,"E3.27.0"),sQuery(id+"F0.wireOp",EDGE,"E3.27.1"),sQuery(id+"F0.wireOp",EDGE,"E3.28.0"),sQuery(id+"F0.wireOp",EDGE,"E3.28.1"),sQuery(id+"F0.wireOp",EDGE,"E3.29.0"),sQuery(id+"F0.wireOp",EDGE,"E3.29.1"),sQuery(id+"F0.wireOp",EDGE,"E3.30.0"),sQuery(id+"F0.wireOp",EDGE,"E3.30.1"),sQuery(id+"F0.wireOp",EDGE,"E3.31.0"),sQuery(id+"F0.wireOp",EDGE,"E3.31.1"),sQuery(id+"F0.wireOp",EDGE,"E3.32.0"),sQuery(id+"F0.wireOp",EDGE,"E3.32.1"),sQuery(id+"F0.wireOp",EDGE,"E3.33.0"),sQuery(id+"F0.wireOp",EDGE,"E3.33.1"),sQuery(id+"F0.wireOp",EDGE,"E3.34.0"),sQuery(id+"F0.wireOp",EDGE,"E3.34.1"),sQuery(id+"F0.wireOp",EDGE,"E3.35.0"),sQuery(id+"F0.wireOp",EDGE,"E3.35.1")])],"isStart":false});
            var Q4;
            Q4=makeQuery(id+"F1.opExtrude","CAP_VERTEX",VERTEX,{"disambiguationData":[OSD([sQuery(id+"F0.wireOp",EDGE,"E3.18.0"),sQuery(id+"F0.wireOp",EDGE,"E3.18.1")])],"isStart":false});
            var Q5;
            Q5=makeQuery(id+"F1.opExtrude","CAP_VERTEX",VERTEX,{"disambiguationData":[OSD([sQuery(id+"F0.wireOp",EDGE,"E3.22.0"),sQuery(id+"F0.wireOp",EDGE,"E3.22.1")])],"isStart":true});
            var Q6;
            Q6=makeQuery(id+"F4.opExtrude","CAP_VERTEX",VERTEX,{"disambiguationData":[OSD([sQuery(id+"F0.wireOp",EDGE,"E3.25.0"),sQuery(id+"F0.wireOp",EDGE,"E3.25.1")])],"isStart":false});
            loft(context, id + "F5", {"startCondition" : LoftEndDerivativeType.MATCH_TANGENT, "startMagnitude" : .1, "endCondition" : LoftEndDerivativeType.TANGENT_TO_PROFILE, "endMagnitude" : .25, "sheetProfilesArray" : [{ "sheetProfileEntities" : qUnion([Q1]) }, { "sheetProfileEntities" : qUnion([Q2]) }, { "sheetProfileEntities" : qUnion([Q3]) }], "matchConnections" : true, "connections" : [{ "connectionEntities" : qUnion([Q4, Q5, Q6]), "connectionEdgeQueries" : qUnion([]), "connectionEdgeParameters" : [] }]});
        }
        {
            var Q0;
            {var subQ0=sQuery(id+"F0.wireOp",EDGE,"E3.35.1");var subQ1=sQuery(id+"F0.wireOp",EDGE,"E3.35.0");var subQ2=sQuery(id+"F0.wireOp",EDGE,"E3.34.1");var subQ3=sQuery(id+"F0.wireOp",EDGE,"E3.34.0");var subQ4=sQuery(id+"F0.wireOp",EDGE,"E3.33.1");var subQ5=sQuery(id+"F0.wireOp",EDGE,"E3.33.0");var subQ6=sQuery(id+"F0.wireOp",EDGE,"E3.32.1");var subQ7=sQuery(id+"F0.wireOp",EDGE,"E3.32.0");var subQ8=sQuery(id+"F0.wireOp",EDGE,"E3.31.1");var subQ9=sQuery(id+"F0.wireOp",EDGE,"E3.31.0");var subQ10=sQuery(id+"F0.wireOp",EDGE,"E3.30.1");var subQ11=sQuery(id+"F0.wireOp",EDGE,"E3.30.0");var subQ12=sQuery(id+"F0.wireOp",EDGE,"E3.29.1");var subQ13=sQuery(id+"F0.wireOp",EDGE,"E3.29.0");var subQ14=sQuery(id+"F0.wireOp",EDGE,"E3.28.1");var subQ15=sQuery(id+"F0.wireOp",EDGE,"E3.28.0");var subQ16=sQuery(id+"F0.wireOp",EDGE,"E3.27.1");var subQ17=sQuery(id+"F0.wireOp",EDGE,"E3.27.0");var subQ18=sQuery(id+"F0.wireOp",EDGE,"E3.26.1");var subQ19=sQuery(id+"F0.wireOp",EDGE,"E3.26.0");var subQ20=sQuery(id+"F0.wireOp",EDGE,"E3.25.1");var subQ21=sQuery(id+"F0.wireOp",EDGE,"E3.25.0");var subQ22=sQuery(id+"F0.wireOp",EDGE,"E3.24.1");var subQ23=sQuery(id+"F0.wireOp",EDGE,"E3.24.0");var subQ24=sQuery(id+"F0.wireOp",EDGE,"E3.23.1");var subQ25=sQuery(id+"F0.wireOp",EDGE,"E3.23.0");var subQ26=sQuery(id+"F0.wireOp",EDGE,"E3.22.1");var subQ27=sQuery(id+"F0.wireOp",EDGE,"E3.22.0");var subQ28=sQuery(id+"F0.wireOp",EDGE,"E3.21.1");var subQ29=sQuery(id+"F0.wireOp",EDGE,"E3.21.0");var subQ30=sQuery(id+"F0.wireOp",EDGE,"E3.20.1");var subQ31=sQuery(id+"F0.wireOp",EDGE,"E3.20.0");var subQ32=sQuery(id+"F0.wireOp",EDGE,"E3.19.1");var subQ33=sQuery(id+"F0.wireOp",EDGE,"E3.19.0");var subQ34=sQuery(id+"F0.wireOp",EDGE,"E3.18.1");var subQ35=sQuery(id+"F0.wireOp",EDGE,"E3.18.0");var subQ36=sQuery(id+"F0.wireOp",EDGE,"E3.17.1");var subQ37=sQuery(id+"F0.wireOp",EDGE,"E3.17.0");var subQ38=sQuery(id+"F0.wireOp",EDGE,"E3.16.1");var subQ39=sQuery(id+"F0.wireOp",EDGE,"E3.16.0");var subQ40=sQuery(id+"F0.wireOp",EDGE,"E3.15.1");var subQ41=sQuery(id+"F0.wireOp",EDGE,"E3.15.0");var subQ42=sQuery(id+"F0.wireOp",EDGE,"E3.14.1");var subQ43=sQuery(id+"F0.wireOp",EDGE,"E3.14.0");var subQ44=sQuery(id+"F0.wireOp",EDGE,"E3.13.1");var subQ45=sQuery(id+"F0.wireOp",EDGE,"E3.13.0");var subQ46=sQuery(id+"F0.wireOp",EDGE,"E3.12.1");var subQ47=sQuery(id+"F0.wireOp",EDGE,"E3.12.0");var subQ48=sQuery(id+"F0.wireOp",EDGE,"E3.11.1");var subQ49=sQuery(id+"F0.wireOp",EDGE,"E3.11.0");var subQ50=sQuery(id+"F0.wireOp",EDGE,"E3.10.1");var subQ51=sQuery(id+"F0.wireOp",EDGE,"E3.10.0");var subQ52=sQuery(id+"F0.wireOp",EDGE,"E3.9.1");var subQ53=sQuery(id+"F0.wireOp",EDGE,"E3.9.0");var subQ54=sQuery(id+"F0.wireOp",EDGE,"E3.8.1");var subQ55=sQuery(id+"F0.wireOp",EDGE,"E3.8.0");var subQ56=sQuery(id+"F0.wireOp",EDGE,"E3.7.1");var subQ57=sQuery(id+"F0.wireOp",EDGE,"E3.7.0");var subQ58=sQuery(id+"F0.wireOp",EDGE,"E3.6.1");var subQ59=sQuery(id+"F0.wireOp",EDGE,"E3.6.0");var subQ60=sQuery(id+"F0.wireOp",EDGE,"E3.5.1");var subQ61=sQuery(id+"F0.wireOp",EDGE,"E3.5.0");var subQ62=sQuery(id+"F0.wireOp",EDGE,"E3.4.1");var subQ63=sQuery(id+"F0.wireOp",EDGE,"E3.4.0");var subQ64=sQuery(id+"F0.wireOp",EDGE,"E3.3.1");var subQ65=sQuery(id+"F0.wireOp",EDGE,"E3.3.0");var subQ66=sQuery(id+"F0.wireOp",EDGE,"E3.2.1");var subQ67=sQuery(id+"F0.wireOp",EDGE,"E3.2.0");var subQ68=sQuery(id+"F0.wireOp",EDGE,"E3.1.1");var subQ69=sQuery(id+"F0.wireOp",EDGE,"E3.1.0");var subQ70=sQuery(id+"F0.wireOp",EDGE,"E2.MirrorCS");var subQ71=sQuery(id+"F0.wireOp",EDGE,"E1");Q0=makeQuery(id+"F5.opLoft","CAP_FACE",FACE,{"disambiguationData":[OSD([subQ71,subQ70,subQ69,subQ68,subQ67,subQ66,subQ65,subQ64,subQ63,subQ62,subQ61,subQ60,subQ59,subQ58,subQ57,subQ56,subQ55,subQ54,subQ53,subQ52,subQ51,subQ50,subQ49,subQ48,subQ47,subQ46,subQ45,subQ44,subQ43,subQ42,subQ41,subQ40,subQ39,subQ38,subQ37,subQ36,subQ35,subQ34,subQ33,subQ32,subQ31,subQ30,subQ29,subQ28,subQ27,subQ26,subQ25,subQ24,subQ23,subQ22,subQ21,subQ20,subQ19,subQ18,subQ17,subQ16,subQ15,subQ14,subQ13,subQ12,subQ11,subQ10,subQ9,subQ8,subQ7,subQ6,subQ5,subQ4,subQ3,subQ2,subQ1,subQ0]),TDD([makeQuery(id+"F1.opExtrude","CAP_FACE",FACE,{"disambiguationData":[OSD([subQ71,subQ70,subQ69,subQ68,subQ67,subQ66,subQ65,subQ64,subQ63,subQ62,subQ61,subQ60,subQ59,subQ58,subQ57,subQ56,subQ55,subQ54,subQ53,subQ52,subQ51,subQ50,subQ49,subQ48,subQ47,subQ46,subQ45,subQ44,subQ43,subQ42,subQ41,subQ40,subQ39,subQ38,subQ37,subQ36,subQ35,subQ34,subQ33,subQ32,subQ31,subQ30,subQ29,subQ28,subQ27,subQ26,subQ25,subQ24,subQ23,subQ22,subQ21,subQ20,subQ19,subQ18,subQ17,subQ16,subQ15,subQ14,subQ13,subQ12,subQ11,subQ10,subQ9,subQ8,subQ7,subQ6,subQ5,subQ4,subQ3,subQ2,subQ1,subQ0])],"isStart":false})])],"isStart":true});}
            var sketch = newSketch(context, id + "F6", { "sketchPlane" : qUnion([Q0])});
            skCircle(sketch, "E4", {"center": v(0, 0) * mm, "radius": 17.5 * mm});
            skCircle(sketch, "E5", {"center": v(28.05, 0) * mm, "radius": 4 * mm});
            skLineSegment(sketch, "E6", {"start": v(38.6, 0) * mm, "end": v(17.5, 0) * mm, "construction": true});
            skCircle(sketch, "E7.1.0", {"center": v(14.02, 24.29) * mm, "radius": 4 * mm});
            skCircle(sketch, "E7.2.0", {"center": v(-14.02, 24.29) * mm, "radius": 4 * mm});
            skCircle(sketch, "E7.3.0", {"center": v(-28.05, 0) * mm, "radius": 4 * mm});
            skCircle(sketch, "E7.4.0", {"center": v(-14.02, -24.29) * mm, "radius": 4 * mm});
            skCircle(sketch, "E7.5.0", {"center": v(14.02, -24.29) * mm, "radius": 4 * mm});
            skSolve(sketch);
        }
        {
            var Q0;
            Q0 = qSketchRegion(id + "F6", true);
            extrude(context, id + "F7", {"entities" : qUnion([Q0]), "operationType" : NewBodyOperationType.REMOVE, "oppositeDirection" : true, "depth" : 1.2 * mm});
        }
    });
